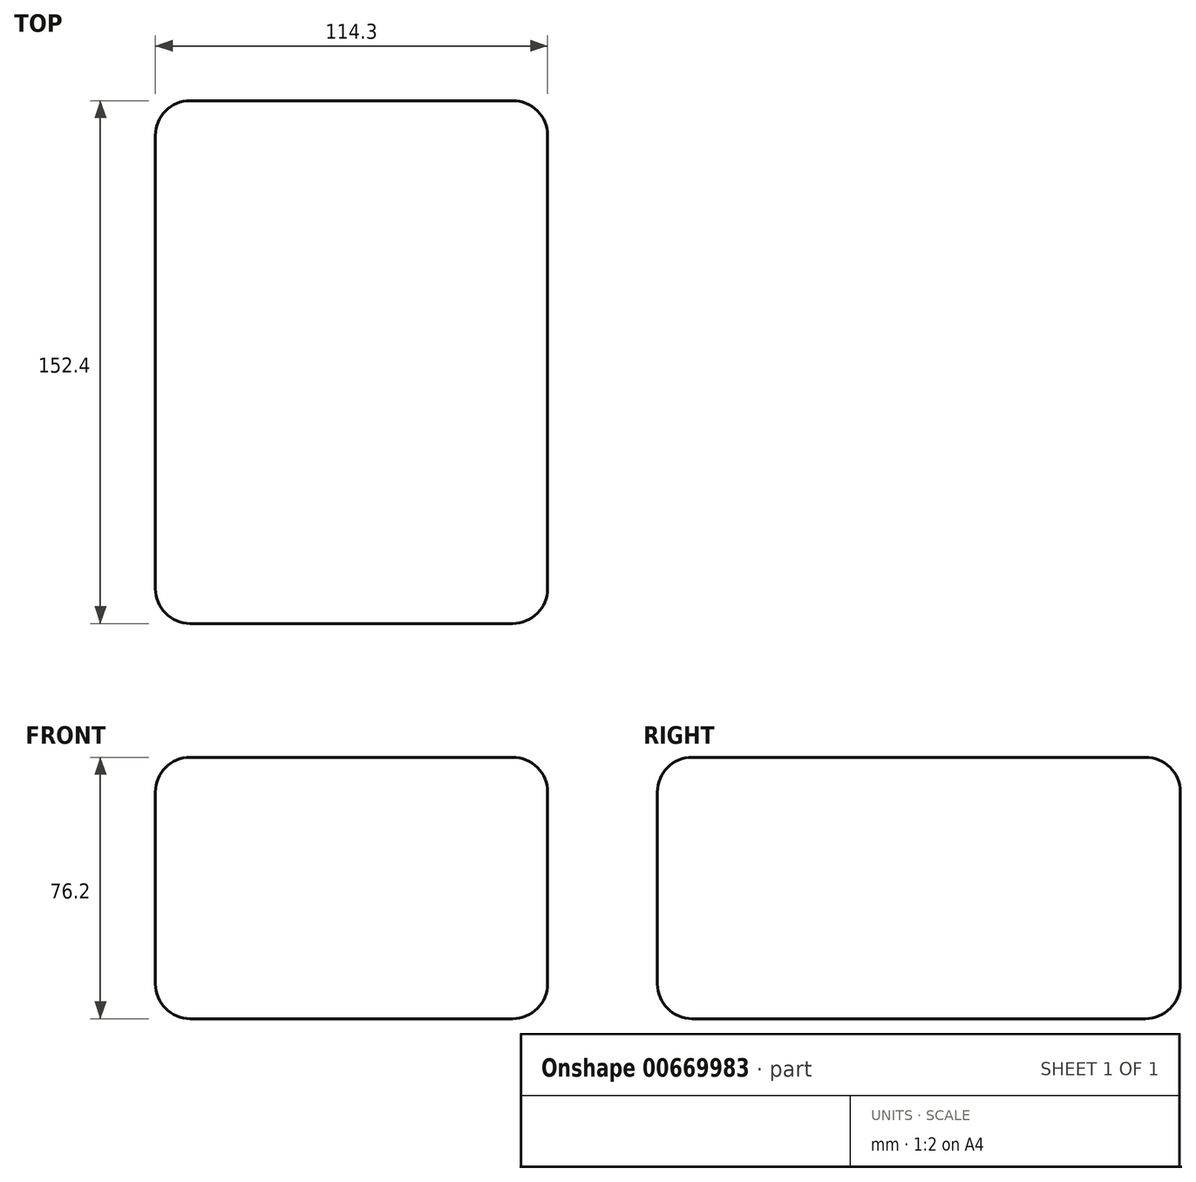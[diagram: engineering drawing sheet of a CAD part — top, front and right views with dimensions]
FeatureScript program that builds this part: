
annotation { "Feature Type Name" : "Feature", "Feature Type Description" : "" }
export const myFeature = defineFeature(function(context is Context, id is Id, definition is map)
    precondition{}
    {
        {
            var Q0;
            Q0=qCreatedBy(makeId("Front.planeOp"),FACE);
            var sketch = newSketch(context, id + "F0", { "sketchPlane" : qUnion([Q0])});
            skLineSegment(sketch, "E0.bottom", {"start": v(57.15, -38.1) * mm, "end": v(-57.15, -38.1) * mm});
            skLineSegment(sketch, "E0.top", {"start": v(57.15, 38.1) * mm, "end": v(-57.15, 38.1) * mm});
            skLineSegment(sketch, "E0.left", {"start": v(57.15, -38.1) * mm, "end": v(57.15, 38.1) * mm});
            skLineSegment(sketch, "E0.right", {"start": v(-57.15, -38.1) * mm, "end": v(-57.15, 38.1) * mm});
            skPoint(sketch, "E0.middle", {"position": v(0, 0) * mm});
            skSolve(sketch);
        }
        {
            var Q0;
            Q0 = qSketchRegion(id + "F0", true);
            extrude(context, id + "F1", {"entities" : qUnion([Q0]), "depth" : 76.2 * mm, "offsetDistance" : 25.4 * mm, "hasSecondDirection" : true, "secondDirectionOppositeDirection" : true, "secondDirectionDepth" : 76.2 * mm});
        }
        {
            var Q0;
            Q0=makeQuery(id+"F1.opExtrude","CAP_EDGE",EDGE,{"disambiguationData":[OSD([sQuery(id+"F0.wireOp",EDGE,"E0.top")])],"isStart":false});
            var Q1;
            Q1=makeQuery(id+"F1.opExtrude","SWEPT_EDGE",EDGE,{"disambiguationData":[OSD([sQuery(id+"F0.wireOp",EDGE,"E0.top"),sQuery(id+"F0.wireOp",EDGE,"E0.left")])]});
            var Q2;
            Q2=makeQuery(id+"F1.opExtrude","CAP_EDGE",EDGE,{"disambiguationData":[OSD([sQuery(id+"F0.wireOp",EDGE,"E0.top")])],"isStart":true});
            var Q3;
            Q3=makeQuery(id+"F1.opExtrude","SWEPT_FACE",FACE,{"disambiguationData":[OSD([sQuery(id+"F0.wireOp",EDGE,"E0.top")])]});
            var Q4;
            Q4=makeQuery(id+"F1.opExtrude","SWEPT_FACE",FACE,{"disambiguationData":[OSD([sQuery(id+"F0.wireOp",EDGE,"E0.left")])]});
            var Q5;
            Q5=makeQuery(id+"F1.opExtrude","CAP_EDGE",EDGE,{"disambiguationData":[OSD([sQuery(id+"F0.wireOp",EDGE,"E0.right")])],"isStart":false});
            var Q6;
            Q6=makeQuery(id+"F1.opExtrude","CAP_FACE",FACE,{"disambiguationData":[OSD([sQuery(id+"F0.wireOp",EDGE,"E0.bottom"),sQuery(id+"F0.wireOp",EDGE,"E0.top"),sQuery(id+"F0.wireOp",EDGE,"E0.left"),sQuery(id+"F0.wireOp",EDGE,"E0.right")])],"isStart":true});
            var Q7;
            Q7=makeQuery(id+"F1.opExtrude","SWEPT_EDGE",EDGE,{"disambiguationData":[OSD([sQuery(id+"F0.wireOp",EDGE,"E0.bottom"),sQuery(id+"F0.wireOp",EDGE,"E0.right")])]});
            var Q8;
            Q8=makeQuery(id+"F1.opExtrude","CAP_EDGE",EDGE,{"disambiguationData":[OSD([sQuery(id+"F0.wireOp",EDGE,"E0.bottom")])],"isStart":false});
            fillet(context, id + "F2", {"entities" : qUnion([Q0, Q1, Q2, Q3, Q4, Q5, Q6, Q7, Q8]), "radius" : 10.16 * mm, "tangentPropagation" : true, "allowEdgeOverflow" : false});
        }
    });
